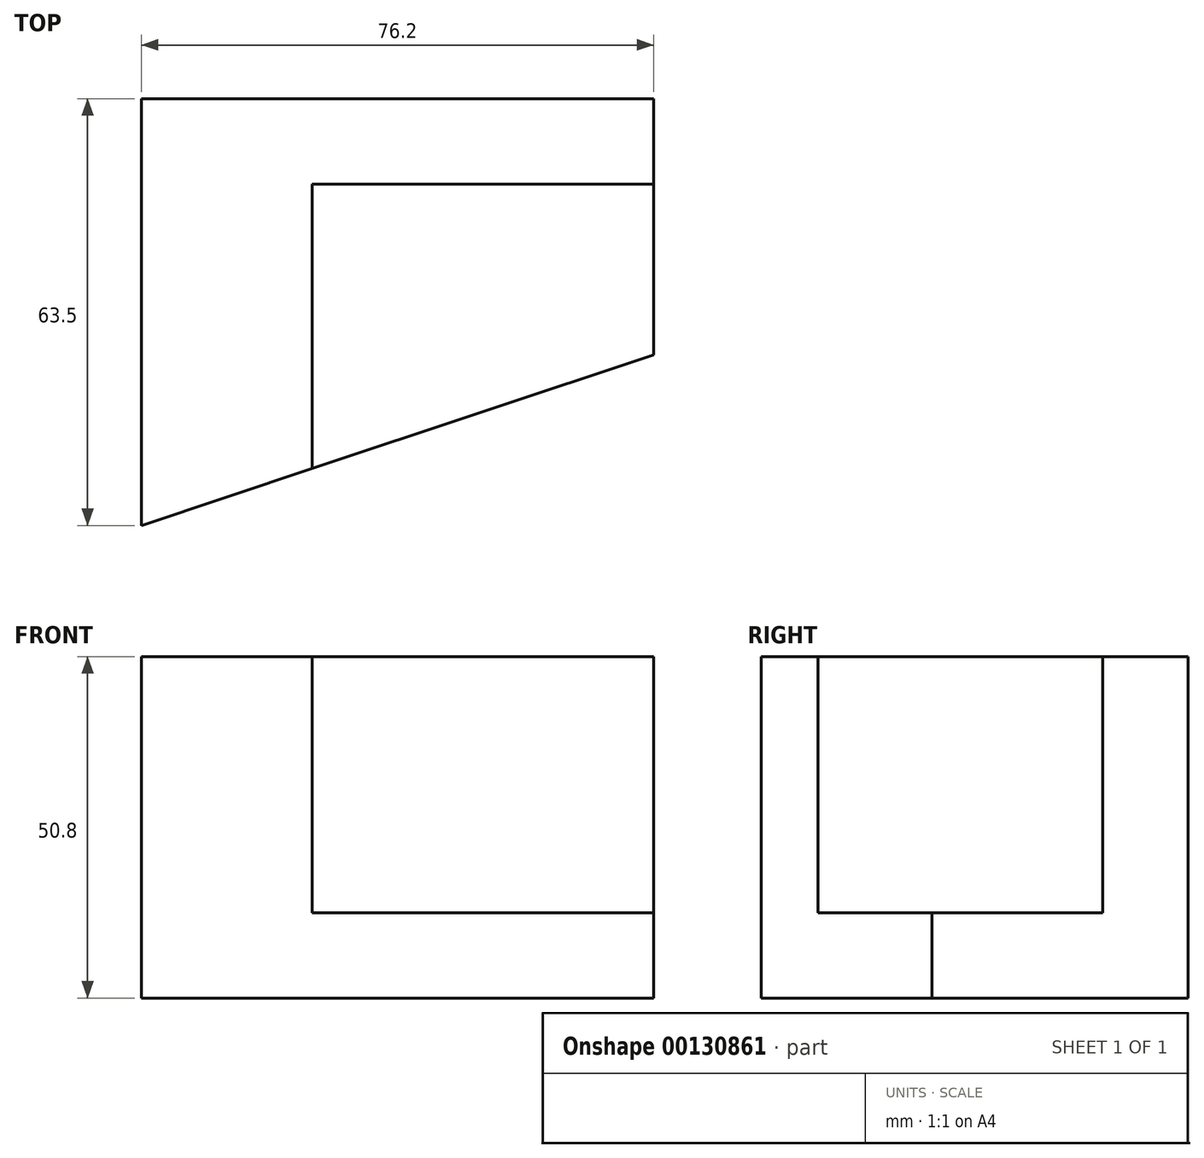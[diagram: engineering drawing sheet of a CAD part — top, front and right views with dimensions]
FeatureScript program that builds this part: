
annotation { "Feature Type Name" : "Feature", "Feature Type Description" : "" }
export const myFeature = defineFeature(function(context is Context, id is Id, definition is map)
    precondition{}
    {
        {
            var Q0;
            Q0=qCreatedBy(makeId("Front.planeOp"),FACE);
            var sketch = newSketch(context, id + "F0", { "sketchPlane" : qUnion([Q0])});
            skLineSegment(sketch, "E0.bottom", {"start": v(0, 0) * mm, "end": v(76.2, 0) * mm});
            skLineSegment(sketch, "E0.top", {"start": v(0, 50.8) * mm, "end": v(76.2, 50.8) * mm});
            skLineSegment(sketch, "E0.left", {"start": v(0, 0) * mm, "end": v(0, 50.8) * mm});
            skLineSegment(sketch, "E0.right", {"start": v(76.2, 0) * mm, "end": v(76.2, 50.8) * mm});
            skSolve(sketch);
        }
        {
            var Q0;
            Q0 = qSketchRegion(id + "F0", true);
            extrude(context, id + "F1", {"entities" : qUnion([Q0]), "oppositeDirection" : true, "depth" : 63.5 * mm});
        }
        {
            var Q0;
            Q0=qCreatedBy(makeId("Top.planeOp"),FACE);
            var sketch = newSketch(context, id + "F2", { "sketchPlane" : qUnion([Q0])});
            skLineSegment(sketch, "E1", {"start": v(0, 0) * mm, "end": v(76.2, 25.4) * mm});
            skLineSegment(sketch, "E2", {"start": v(76.2, 0) * mm, "end": v(76.2, 25.4) * mm});
            skLineSegment(sketch, "E3", {"start": v(76.2, 0) * mm, "end": v(0, 0) * mm});
            skSolve(sketch);
        }
        {
            var Q0;
            Q0 = qSketchRegion(id + "F2", true);
            extrude(context, id + "F3", {"entities" : qUnion([Q0]), "operationType" : NewBodyOperationType.REMOVE, "endBound" : BoundingType.THROUGH_ALL, "depth" : 25.4 * mm});
        }
        {
            var Q0;
            Q0=qCreatedBy(makeId("Front.planeOp"),FACE);
            var sketch = newSketch(context, id + "F4", { "sketchPlane" : qUnion([Q0])});
            skLineSegment(sketch, "E4.bottom", {"start": v(76.2, 12.7) * mm, "end": v(25.4, 12.7) * mm});
            skLineSegment(sketch, "E4.top", {"start": v(76.2, 50.8) * mm, "end": v(25.4, 50.8) * mm});
            skLineSegment(sketch, "E4.left", {"start": v(76.2, 12.7) * mm, "end": v(76.2, 50.8) * mm});
            skLineSegment(sketch, "E4.right", {"start": v(25.4, 12.7) * mm, "end": v(25.4, 50.8) * mm});
            skSolve(sketch);
        }
        {
            var Q0;
            Q0 = qSketchRegion(id + "F4", true);
            extrude(context, id + "F5", {"entities" : qUnion([Q0]), "operationType" : NewBodyOperationType.REMOVE, "oppositeDirection" : true, "depth" : 50.8 * mm});
        }
    });
